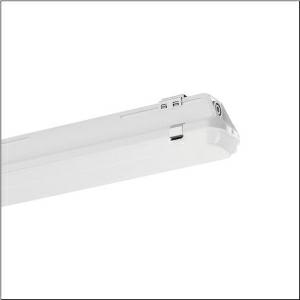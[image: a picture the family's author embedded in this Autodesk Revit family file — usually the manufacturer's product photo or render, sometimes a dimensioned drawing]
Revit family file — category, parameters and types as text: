
# Revit family: monsun_r__11_51fp10mp4b0u_8639
name_source: partatom
category: Lighting Fixtures
units: mm (PartAtom-declared; Revit-internal decimal feet)

## family parameters
Cut with Voids When Loaded = No
Host = Face
Light Source = No
Part Type = Normal
Room Calculation Point = No
Round Connector Dimension = Use Diameter
Shared = No

## types (1)
- --- (1 x LED, 12070 lm, 62.4 W, 4000K)
    Apparent Load = 62 VA
    CIE Flux Codes = 47 76 93 94 100
    Color Rendering = 80
    Color Temperature = 4000K
    Default Elevation = 1800 mm
    Description = Monsun® 11, damp-proof luminaire, chain hanger, primary optical cover: enclosure, of PMMA, light emission: direct distribution, primary light characteristic: symmetric, installation type: suspended mounting, surface-mounted, horizontal mounting, vertical mounting, LED, rated luminous flux: 12.070lm, luminous efficacy: 193lm/W, light colour: 840, colour temperature: 4000K, control gear: ON/OFF Multilumen, with terminal, 3-pole, max. 2.5mm², mains connection: 220..240V, AC, 50/60Hz, rated input power: 62W, luminaire housing, of glass-fibre reinforced polyester, uncoated, bright grey, incl. chain hanger, length: 1.590mm, width: 90mm, height: 88mm, clip for enclosure, of stainless steel (V2A), ceiling mounting element, of stainless steel (V2A), chain hanger, of stainless steel (V2A), protection rating (complete): IP66, insulation class (complete): insulation class I (protective earthing), certification: CE, ENEC, VDE, UKCA, protection symbol: D, impact resistance: IK04, permissible operating ambient temperature: -35..+35°C, standard: EN 50419, EN 60598-2-1, contact your sales advisor before using the luminaires in applications with unclear chemical exposure, large temperature fluctuations or condensation-forming humidity, LABS conformity tested according to VDMA 24364:2018-05, no direct snow, no direct sun, no direct rain, for indoor or canopied outdoor use, corresponds to IFS (International Featured Standards) requirements for safety and quality in the food industry, packaging unit: 1 piece
    Height = 89 mm
    Lamp = 1 x LED
    Lamp Light Flux = 12070 lm
    Lamp Power = 62.4 W
    Lamp count = 1
    Length = 1590 mm
    Luminous efficacy = 193 lm/W
    Manufacturer = Siteco
    ModVariant = No
    Model = 51FP10MP4B0U
    Mounting Place = Ceiling
    Mounting Type = Surface mounted
    Number of Poles = 1
    OnlyDefault = Yes
    Power Factor = 1
    Product Name = Monsun® 11
    Product group = damp-proof luminaire
    ProductGroupID = 301
    Protection Class = Protection class I
    Protection Degree = IP 66
    RLX_Detail_Level = 1
    RLX_Emergency_Light_Flux = 0 lm
    RLX_Emergency_Type = 0
    RLX_Emergency_Type_DB = No
    RlxData = <blob elided: 90061 chars, md5=acc895bf>
    Socket = socket
    Standby Power = 0 W
    System Light Flux = 12070 lm
    System Power = 62 W
    Type Comments = factory setting: luminous flux: 100 % | (A | C | E) | 147 mA
    Type Image = l_1349237.jpg
    URL = http://relux.com
    VarID = @adj_038675
    Voltage = 0 V
    Weight = 0.00 kg
    Width = 90 mm

## geometry (parser evidence)
native form markers: Blend x4, Sweep x15
no freeform markers — native parametric forms only
